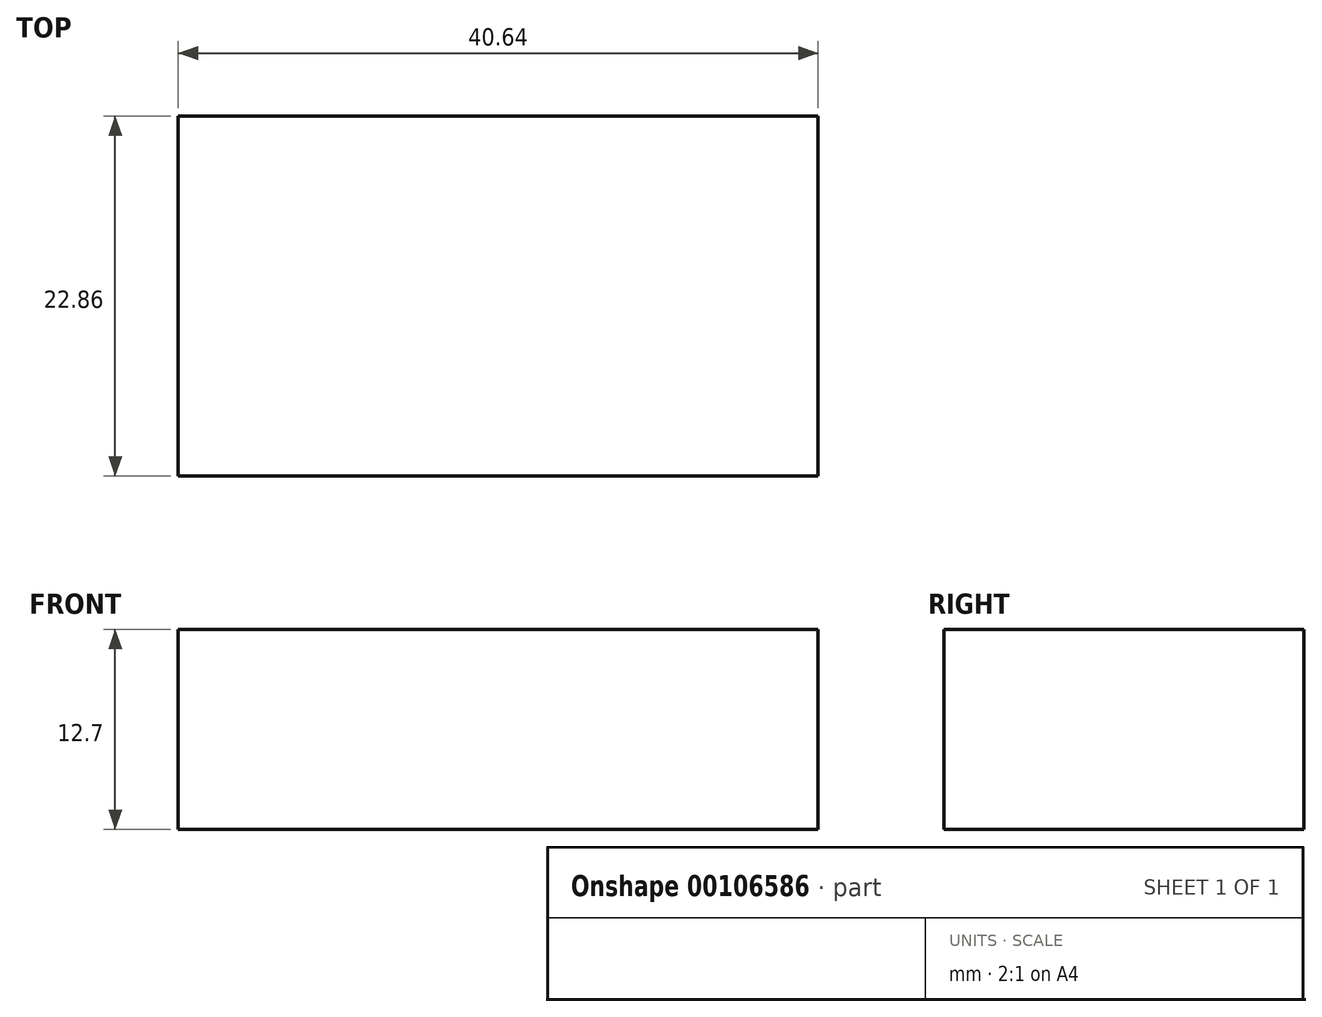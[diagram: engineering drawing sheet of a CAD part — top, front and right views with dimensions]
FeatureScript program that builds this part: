
annotation { "Feature Type Name" : "Feature", "Feature Type Description" : "" }
export const myFeature = defineFeature(function(context is Context, id is Id, definition is map)
    precondition{}
    {
        {
            var Q0;
            Q0=qCreatedBy(makeId("Top.planeOp"),FACE);
            var sketch = newSketch(context, id + "F0", { "sketchPlane" : qUnion([Q0])});
            skLineSegment(sketch, "E0.bottom", {"start": v(-40.74, 27.85) * mm, "end": v(-0.1, 27.85) * mm});
            skLineSegment(sketch, "E0.top", {"start": v(-40.74, 4.99) * mm, "end": v(-0.1, 4.99) * mm});
            skLineSegment(sketch, "E0.left", {"start": v(-40.74, 27.85) * mm, "end": v(-40.74, 4.99) * mm});
            skLineSegment(sketch, "E0.right", {"start": v(-0.1, 27.85) * mm, "end": v(-0.1, 4.99) * mm});
            skSolve(sketch);
        }
        {
            var Q0;
            Q0=makeQuery(id+"F0.imprint","IMPRINT",FACE,{"disambiguationData":[TD([[makeQuery(id+"F0.imprint","IMPRINT",EDGE,{"derivedFrom":sQuery(id+"F0.wireOp",EDGE,"E0.bottom")}),-1.0]])]});
            extrude(context, id + "F1", {"entities" : qUnion([Q0]), "depth" : 12.7 * mm});
        }
    });
